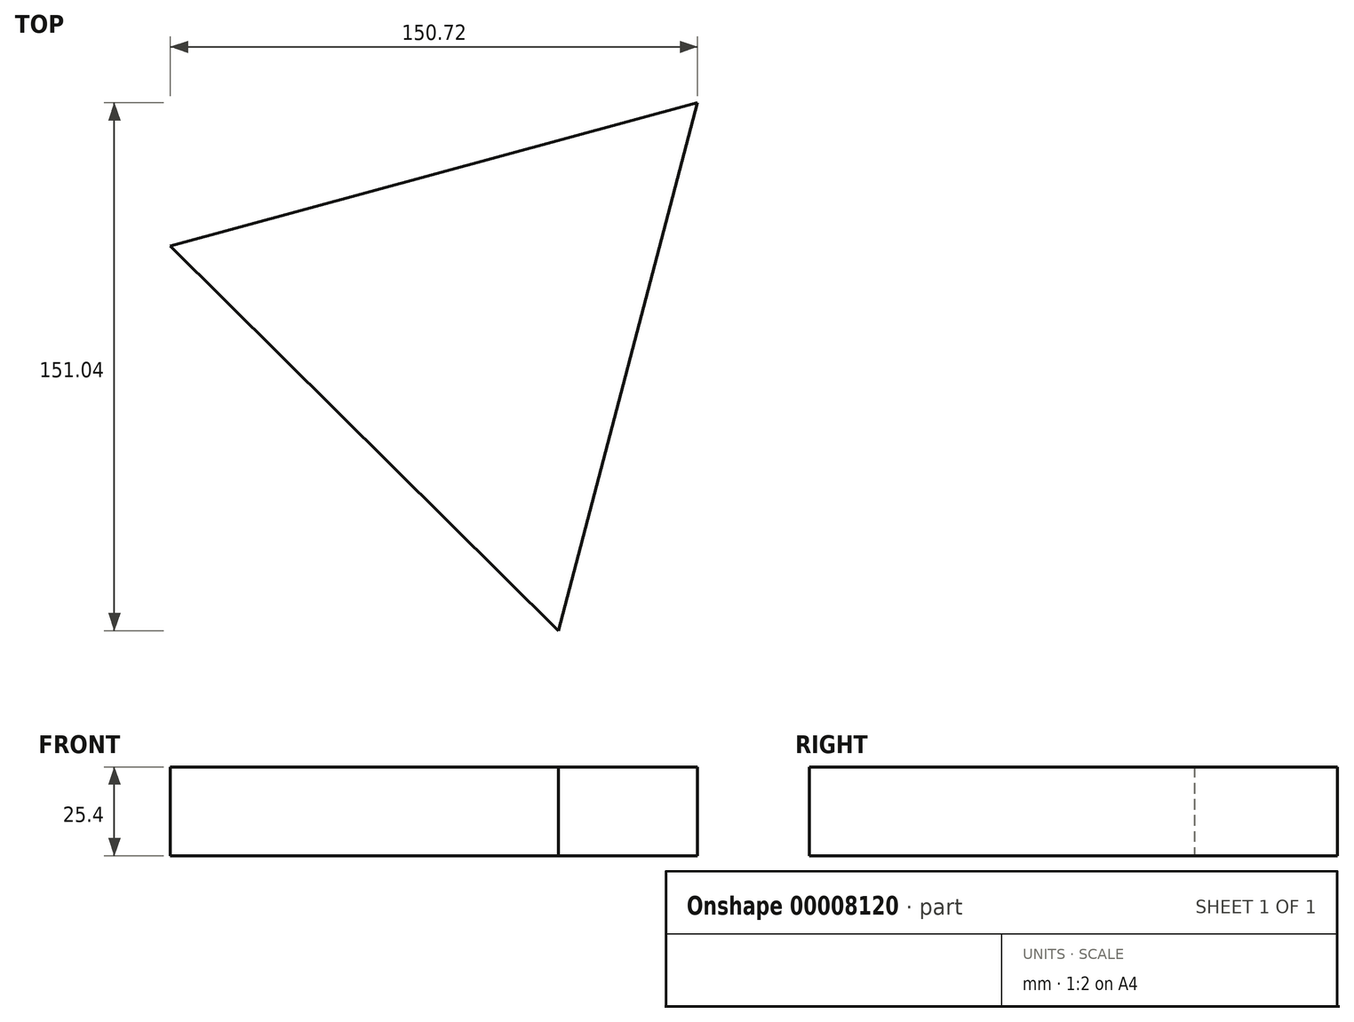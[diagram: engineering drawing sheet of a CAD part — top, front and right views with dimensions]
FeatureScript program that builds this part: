
annotation { "Feature Type Name" : "Feature", "Feature Type Description" : "" }
export const myFeature = defineFeature(function(context is Context, id is Id, definition is map)
    precondition{}
    {
        {
            var Q0;
            Q0=qCreatedBy(makeId("Top.planeOp"),FACE);
            var sketch = newSketch(context, id + "F0", { "sketchPlane" : qUnion([Q0])});
            skCircle(sketch, "E0.cCircle", {"center": v(-53.32, -17.32) * mm, "radius": 45.1 * mm, "construction": true});
            skLineSegment(sketch, "E0.0", {"start": v(10.2, 46.7) * mm, "end": v(-29.64, -104.34) * mm});
            skLineSegment(sketch, "E0.1", {"start": v(-29.64, -104.34) * mm, "end": v(-140.52, 5.68) * mm});
            skLineSegment(sketch, "E0.2", {"start": v(-140.52, 5.68) * mm, "end": v(10.2, 46.7) * mm});
            skPoint(sketch, "E0.0.midPoint", {"position": v(-9.72, -28.82) * mm});
            skSolve(sketch);
        }
        {
            var Q0;
            Q0=makeQuery(id+"F0.imprint","IMPRINT",FACE,{"disambiguationData":[TD([[makeQuery(id+"F0.imprint","IMPRINT",EDGE,{"derivedFrom":sQuery(id+"F0.wireOp",EDGE,"E0.0")}),-1.0]])]});
            extrude(context, id + "F1", {"entities" : qUnion([Q0]), "depth" : 25.4 * mm});
        }
    });
